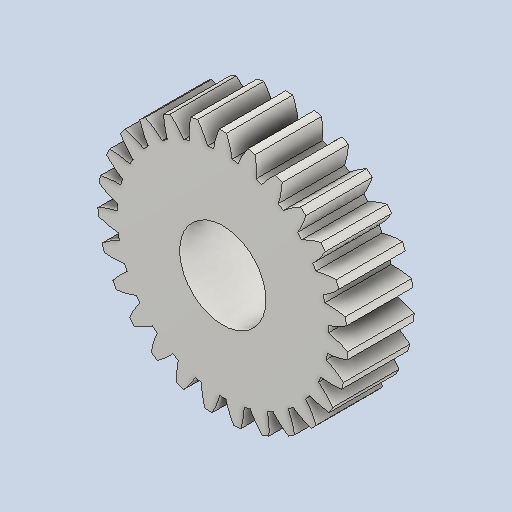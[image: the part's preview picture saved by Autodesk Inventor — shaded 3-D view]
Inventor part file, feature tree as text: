
AUTODESK INVENTOR PART (.ipt)
format: ipt  version: 2022 (Build 260153000, 153)  size: 291,328 bytes
history: native  units: mm (DEFAULTED — no unit token found)
features: plane x3, other x3, sketch x2, extrude x1
ambient origin geometry x8: Origin, YZ Plane, XZ Plane, XY Plane, X Axis, Y Axis, Z Axis, Center Point
bodies: Solid1 (feature_tree)
feature tree (9):
  extrude  "Extrusion1"  Depth=5.0mm TaperAngle=0.0deg
  plane  "Work Plane2"
  plane  "Work Plane8"
  plane  "Work Plane9"
  other  "Spur Gear"
  sketch  "Sketch1"  dims[d0=18.843557mm d1=5.0mm d2=0.0mm]
  sketch  "Sketch2"  dims[d3=17.55mm d4=10.0mm d5=0.0mm d16=18.0mm d17=0.0mm d34=1.163553mm d39=0.0mm d41=0.0mm d43=18.0mm d46=18.0mm d47=0.0mm d48=0.0mm d49=6.5mm]
  other  "Srf1"
  other  "Pitch Diameter"
